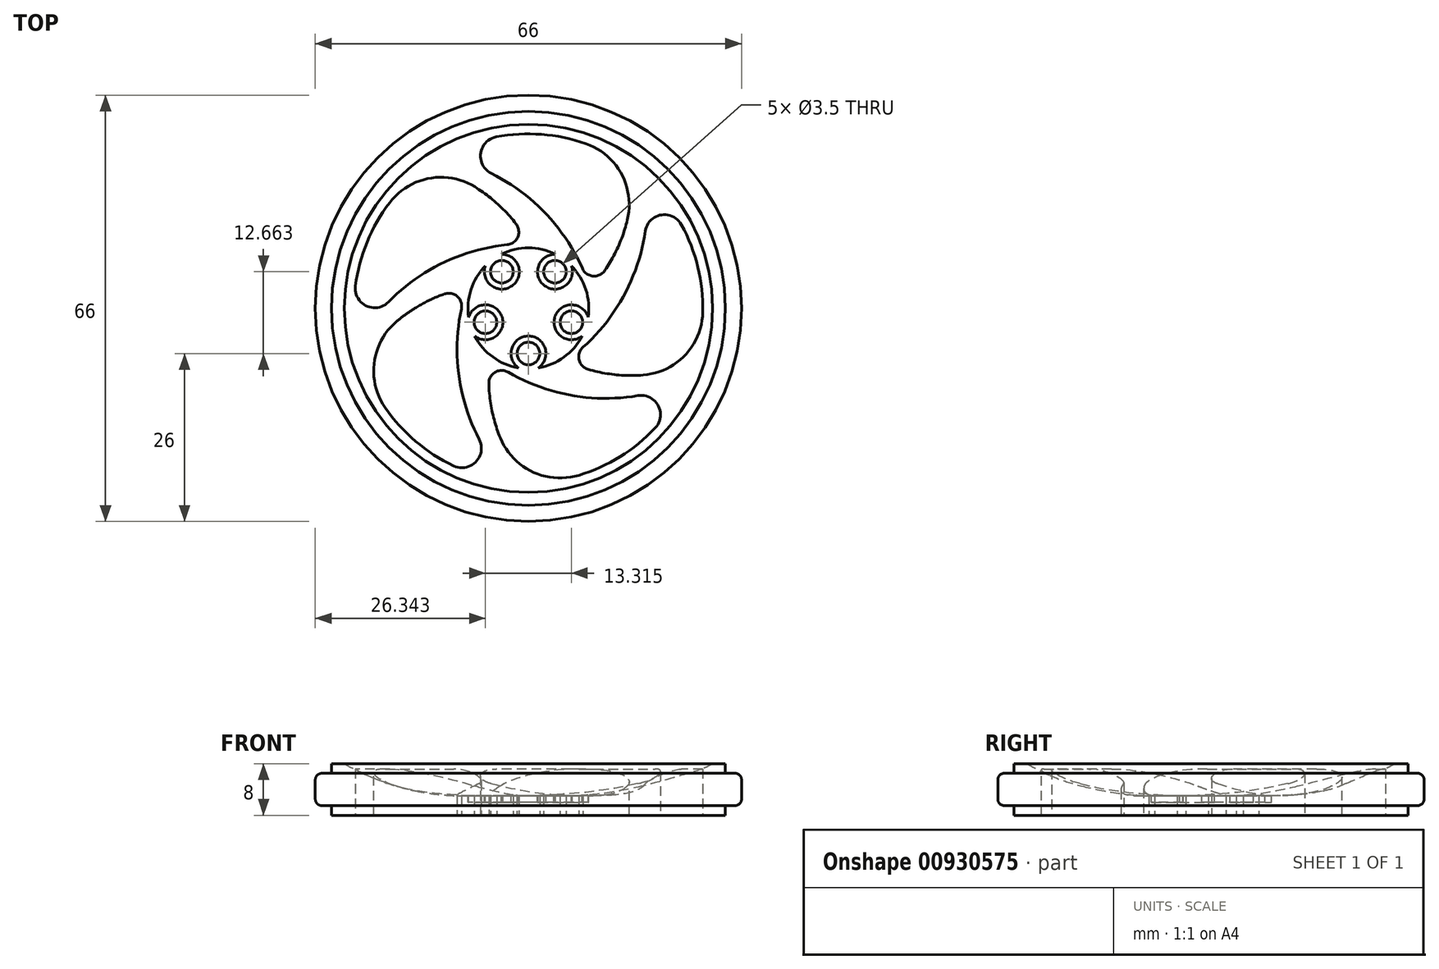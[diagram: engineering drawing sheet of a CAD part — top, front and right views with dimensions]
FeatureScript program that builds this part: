
annotation { "Feature Type Name" : "Feature", "Feature Type Description" : "" }
export const myFeature = defineFeature(function(context is Context, id is Id, definition is map)
    precondition{}
    {
        {
            var Q0;
            Q0=qCreatedBy(makeId("Front.planeOp"),FACE);
            var sketch = newSketch(context, id + "F0", { "sketchPlane" : qUnion([Q0])});
            skLineSegment(sketch, "E0.right", {"start": v(33, 1.5) * mm, "end": v(33, 6.5) * mm});
            skLineSegment(sketch, "E1", {"start": v(30.5, 6.5) * mm, "end": v(33, 6.5) * mm});
            skLineSegment(sketch, "E2", {"start": v(30.5, 6.5) * mm, "end": v(30.5, 8) * mm});
            skLineSegment(sketch, "E3.MirrorCS", {"start": v(30.5, 1.5) * mm, "end": v(30.5, 0) * mm});
            skLineSegment(sketch, "E4.MirrorCS", {"start": v(30.5, 1.5) * mm, "end": v(33, 1.5) * mm});
            skLineSegment(sketch, "E5.trimOffspring", {"start": v(28.5, 8) * mm, "end": v(30.5, 8) * mm});
            skLineSegment(sketch, "E6", {"start": v(0, 0) * mm, "end": v(30.5, 0) * mm});
            skLineSegment(sketch, "E7", {"start": v(0, 0) * mm, "end": v(0, 3) * mm});
            skLineSegment(sketch, "E8", {"start": v(0, 3) * mm, "end": v(10, 3) * mm});
            skArc(sketch, "E9", {"start": v(10, 3) * mm, "mid": v(19.58, 4.27) * mm, "end": v(28.5, 8) * mm});
            skSolve(sketch);
        }
        {
            var Q0;
            Q0=qSketchRegion(id+"F0",true);
            var Q1;
            Q1=sQuery(id+"F0.wireOp",EDGE,"E7");
            revolve(context, id + "F1", {"entities" : qUnion([Q0]), "axis" : qUnion([Q1]), "revolveType" : RevolveType.FULL});
        }
        {
            var Q0;
            Q0=makeQuery(id+"F1.opRevolve","SWEPT_EDGE",EDGE,{"disambiguationData":[OSD([sQuery(id+"F0.wireOp",EDGE,"E0.right"),sQuery(id+"F0.wireOp",EDGE,"E1")])]});
            var Q1;
            Q1=makeQuery(id+"F1.opRevolve","SWEPT_EDGE",EDGE,{"disambiguationData":[OSD([sQuery(id+"F0.wireOp",EDGE,"E0.right"),sQuery(id+"F0.wireOp",EDGE,"E4.MirrorCS")])]});
            fillet(context, id + "F2", {"entities" : qUnion([Q0, Q1]), "radius" : 1 * mm, "tangentPropagation" : true, "allowEdgeOverflow" : false});
        }
        {
            var Q0;
            Q0=makeQuery(id+"F1.opRevolve","SWEPT_FACE",FACE,{"disambiguationData":[OSD([sQuery(id+"F0.wireOp",EDGE,"E6")])]});
            var sketch = newSketch(context, id + "F3", { "sketchPlane" : qUnion([Q0])});
            skCircle(sketch, "E10", {"center": v(0, 0) * mm, "radius": 10 * mm, "construction": true});
            skCircle(sketch, "E11", {"center": v(0, 0) * mm, "radius": 28.5 * mm, "construction": true});
            skArc(sketch, "E12", {"start": v(-3, 26.83) * mm, "mid": v(-17.06, 20.93) * mm, "end": v(-25.68, 8.34) * mm});
            skArc(sketch, "E13.trimOffspring", {"start": v(-26.45, 5.44) * mm, "mid": v(-25.18, -9.76) * mm, "end": v(-15.87, -21.84) * mm});
            skArc(sketch, "E14.trimOffspring", {"start": v(18.2, -19.95) * mm, "mid": v(26.1, -6.9) * mm, "end": v(25.68, 8.34) * mm});
            skLineSegment(sketch, "E15", {"start": v(0, 28.5) * mm, "end": v(0, 0) * mm, "construction": true});
            skLineSegment(sketch, "E16", {"start": v(0, 0) * mm, "end": v(-25.68, 8.34) * mm, "construction": true});
            skLineSegment(sketch, "E17", {"start": v(0, 0) * mm, "end": v(25.68, 8.34) * mm, "construction": true});
            skLineSegment(sketch, "E18", {"start": v(0, 0) * mm, "end": v(-15.87, -21.84) * mm, "construction": true});
            skLineSegment(sketch, "E19", {"start": v(0, 0) * mm, "end": v(15.87, -21.84) * mm, "construction": true});
            skArc(sketch, "E20.trimOffspring", {"start": v(24.6, 11.14) * mm, "mid": v(14.63, 22.7) * mm, "end": v(0, 27) * mm});
            skArc(sketch, "E21.trimOffspring", {"start": v(-13.35, -23.47) * mm, "mid": v(1.5, -26.96) * mm, "end": v(15.87, -21.84) * mm});
            skCircle(sketch, "E22", {"center": v(0, 7) * mm, "radius": 1.75 * mm});
            skCircle(sketch, "E23", {"center": v(-4.11, -5.66) * mm, "radius": 1.75 * mm});
            skCircle(sketch, "E24", {"center": v(4.11, -5.66) * mm, "radius": 1.75 * mm});
            skCircle(sketch, "E25", {"center": v(6.66, 2.16) * mm, "radius": 1.75 * mm});
            skCircle(sketch, "E26", {"center": v(-6.66, 2.16) * mm, "radius": 1.75 * mm});
            skArc(sketch, "E27", {"start": v(-3, 26.83) * mm, "mid": v(-10.37, 12.71) * mm, "end": v(-9.48, -3.2) * mm});
            skArc(sketch, "E28", {"start": v(-26.45, 5.44) * mm, "mid": v(-15.3, -5.93) * mm, "end": v(0.1, -10) * mm});
            skArc(sketch, "E29", {"start": v(-13.35, -23.47) * mm, "mid": v(0.92, -16.38) * mm, "end": v(9.54, -2.99) * mm});
            skArc(sketch, "E30", {"start": v(18.2, -19.95) * mm, "mid": v(15.86, -4.19) * mm, "end": v(5.8, 8.15) * mm});
            skArc(sketch, "E31", {"start": v(24.6, 11.14) * mm, "mid": v(8.89, 13.8) * mm, "end": v(-5.96, 8.03) * mm});
            skArc(sketch, "E32", {"start": v(0, 27) * mm, "mid": v(-5.04, 18.16) * mm, "end": v(-5.96, 8.03) * mm});
            skArc(sketch, "E33", {"start": v(-25.68, 8.34) * mm, "mid": v(-18.83, 0.82) * mm, "end": v(-9.48, -3.2) * mm});
            skArc(sketch, "E34", {"start": v(-15.87, -21.84) * mm, "mid": v(-6.6, -17.65) * mm, "end": v(0.1, -10) * mm});
            skArc(sketch, "E35", {"start": v(15.87, -21.84) * mm, "mid": v(14.75, -11.73) * mm, "end": v(9.54, -2.99) * mm});
            skArc(sketch, "E36", {"start": v(25.68, 8.34) * mm, "mid": v(15.71, 10.4) * mm, "end": v(5.8, 8.15) * mm});
            skSolve(sketch);
        }
        {
            var Q0;
            Q0=qSketchRegion(id+"F3",true);
            extrude(context, id + "F4", {"entities" : qUnion([Q0]), "operationType" : NewBodyOperationType.REMOVE, "oppositeDirection" : true, "depth" : 25 * mm});
        }
        {
            var Q0;
            Q0=makeQuery(id+"F4.boolean.opBoolean","COPY",EDGE,{"derivedFrom":makeQuery(id+"F4.opExtrude","SWEPT_EDGE",EDGE,{"disambiguationData":[OSD([sQuery(id+"F3.wireOp",EDGE,"E12"),sQuery(id+"F3.wireOp",EDGE,"E27")])]})});
            var Q1;
            Q1=makeQuery(id+"F4.boolean.opBoolean","COPY",EDGE,{"derivedFrom":makeQuery(id+"F4.opExtrude","SWEPT_EDGE",EDGE,{"disambiguationData":[OSD([sQuery(id+"F3.wireOp",EDGE,"E20.trimOffspring"),sQuery(id+"F3.wireOp",EDGE,"E31")])]})});
            var Q2;
            Q2=makeQuery(id+"F4.boolean.opBoolean","COPY",EDGE,{"derivedFrom":makeQuery(id+"F4.opExtrude","SWEPT_EDGE",EDGE,{"disambiguationData":[OSD([sQuery(id+"F3.wireOp",EDGE,"E14.trimOffspring"),sQuery(id+"F3.wireOp",EDGE,"E30")])]})});
            var Q3;
            Q3=makeQuery(id+"F4.boolean.opBoolean","COPY",EDGE,{"derivedFrom":makeQuery(id+"F4.opExtrude","SWEPT_EDGE",EDGE,{"disambiguationData":[OSD([sQuery(id+"F3.wireOp",EDGE,"E21.trimOffspring"),sQuery(id+"F3.wireOp",EDGE,"E29")])]})});
            var Q4;
            Q4=makeQuery(id+"F4.boolean.opBoolean","COPY",EDGE,{"derivedFrom":makeQuery(id+"F4.opExtrude","SWEPT_EDGE",EDGE,{"disambiguationData":[OSD([sQuery(id+"F3.wireOp",EDGE,"E13.trimOffspring"),sQuery(id+"F3.wireOp",EDGE,"E28")])]})});
            fillet(context, id + "F5", {"entities" : qUnion([Q0, Q1, Q2, Q3, Q4]), "radius" : 3 * mm, "tangentPropagation" : true, "allowEdgeOverflow" : false});
        }
        {
            var Q0;
            Q0=makeQuery(id+"F4.boolean.opBoolean","COPY",EDGE,{"derivedFrom":makeQuery(id+"F4.opExtrude","SWEPT_EDGE",EDGE,{"disambiguationData":[OSD([sQuery(id+"F3.wireOp",EDGE,"E14.trimOffspring"),sQuery(id+"F3.wireOp",EDGE,"lH133nUo-b4dK-7Uis-ALbx-UH7YrD5dzAr5")])]})});
            var Q1;
            Q1=makeQuery(id+"F4.boolean.opBoolean","COPY",EDGE,{"derivedFrom":makeQuery(id+"F4.opExtrude","SWEPT_EDGE",EDGE,{"disambiguationData":[OSD([sQuery(id+"F3.wireOp",EDGE,"E20.trimOffspring"),sQuery(id+"F3.wireOp",EDGE,"Y5TeA7qx-hglw-YKO1-yJVa-Mu3tWydujS0s")])]})});
            var Q2;
            Q2=makeQuery(id+"F4.boolean.opBoolean","COPY",EDGE,{"derivedFrom":makeQuery(id+"F4.opExtrude","SWEPT_EDGE",EDGE,{"disambiguationData":[OSD([sQuery(id+"F3.wireOp",EDGE,"E12"),sQuery(id+"F3.wireOp",EDGE,"K8Gechwi-EIRI-6laA-ybGk-XkUKvmpAPVkA")])]})});
            var Q3;
            Q3=makeQuery(id+"F4.boolean.opBoolean","COPY",EDGE,{"derivedFrom":makeQuery(id+"F4.opExtrude","SWEPT_EDGE",EDGE,{"disambiguationData":[OSD([sQuery(id+"F3.wireOp",EDGE,"E13.trimOffspring"),sQuery(id+"F3.wireOp",EDGE,"yrZSpx71-NN5u-So2I-DmkD-7K2vPXZf8bNT")])]})});
            var Q4;
            Q4=makeQuery(id+"F4.boolean.opBoolean","COPY",EDGE,{"derivedFrom":makeQuery(id+"F4.opExtrude","SWEPT_EDGE",EDGE,{"disambiguationData":[OSD([sQuery(id+"F3.wireOp",EDGE,"E21.trimOffspring"),sQuery(id+"F3.wireOp",EDGE,"3wq5JMd6-PSVr-Z4Na-BiTl-nTZF3QSmccvR")])]})});
            fillet(context, id + "F6", {"entities" : qUnion([Q0, Q1, Q2, Q3, Q4]), "radius" : 10 * mm, "tangentPropagation" : true, "allowEdgeOverflow" : false});
        }
        {
            var Q0;
            Q0=makeQuery(id+"F4.boolean.opBoolean","COPY",EDGE,{"derivedFrom":makeQuery(id+"F4.opExtrude","SWEPT_EDGE",EDGE,{"disambiguationData":[OSD([sQuery(id+"F3.wireOp",EDGE,"E28"),sQuery(id+"F3.wireOp",EDGE,"E34")])]})});
            var Q1;
            Q1=makeQuery(id+"F4.boolean.opBoolean","COPY",EDGE,{"derivedFrom":makeQuery(id+"F4.opExtrude","SWEPT_EDGE",EDGE,{"disambiguationData":[OSD([sQuery(id+"F3.wireOp",EDGE,"E29"),sQuery(id+"F3.wireOp",EDGE,"E35")])]})});
            var Q2;
            Q2=makeQuery(id+"F4.boolean.opBoolean","COPY",EDGE,{"derivedFrom":makeQuery(id+"F4.opExtrude","SWEPT_EDGE",EDGE,{"disambiguationData":[OSD([sQuery(id+"F3.wireOp",EDGE,"E30"),sQuery(id+"F3.wireOp",EDGE,"E36")])]})});
            var Q3;
            Q3=makeQuery(id+"F4.boolean.opBoolean","COPY",EDGE,{"derivedFrom":makeQuery(id+"F4.opExtrude","SWEPT_EDGE",EDGE,{"disambiguationData":[OSD([sQuery(id+"F3.wireOp",EDGE,"E31"),sQuery(id+"F3.wireOp",EDGE,"E32")])]})});
            var Q4;
            Q4=makeQuery(id+"F4.boolean.opBoolean","COPY",EDGE,{"derivedFrom":makeQuery(id+"F4.opExtrude","SWEPT_EDGE",EDGE,{"disambiguationData":[OSD([sQuery(id+"F3.wireOp",EDGE,"E27"),sQuery(id+"F3.wireOp",EDGE,"E33")])]})});
            fillet(context, id + "F7", {"entities" : qUnion([Q0, Q1, Q2, Q3, Q4]), "radius" : 2 * mm, "tangentPropagation" : true, "allowEdgeOverflow" : false});
        }
        {
            var Q0;
            Q0=makeQuery(id+"F1.opRevolve","SWEPT_FACE",FACE,{"disambiguationData":[OSD([sQuery(id+"F0.wireOp",EDGE,"E8")])]});
            var sketch = newSketch(context, id + "F8", { "sketchPlane" : qUnion([Q0])});
            skArc(sketch, "E37", {"start": v(-6.66, 6.56) * mm, "mid": v(-2.53, 3.48) * mm, "end": v(-4.18, 8.36) * mm});
            skArc(sketch, "E38", {"start": v(4.18, 8.36) * mm, "mid": v(2.53, 3.48) * mm, "end": v(6.66, 6.56) * mm});
            skArc(sketch, "E39", {"start": v(9.25, -1.4) * mm, "mid": v(4.09, -1.33) * mm, "end": v(8.3, -4.3) * mm});
            skArc(sketch, "E40", {"start": v(1.53, -9.22) * mm, "mid": v(0, -4.3) * mm, "end": v(-1.53, -9.22) * mm});
            skArc(sketch, "E41", {"start": v(-8.3, -4.3) * mm, "mid": v(-4.09, -1.33) * mm, "end": v(-9.25, -1.4) * mm});
            skArc(sketch, "E42", {"start": v(-6.66, 6.56) * mm, "mid": v(-8.9, 2.89) * mm, "end": v(-9.25, -1.4) * mm});
            skArc(sketch, "E43.trimOffspring", {"start": v(4.18, 8.36) * mm, "mid": v(0, 9.35) * mm, "end": v(-4.18, 8.36) * mm});
            skArc(sketch, "E44.trimOffspring", {"start": v(9.25, -1.4) * mm, "mid": v(8.9, 2.89) * mm, "end": v(6.66, 6.56) * mm});
            skArc(sketch, "E45.trimOffspring", {"start": v(1.53, -9.22) * mm, "mid": v(5.5, -7.56) * mm, "end": v(8.3, -4.3) * mm});
            skArc(sketch, "E46.trimOffspring", {"start": v(-8.3, -4.3) * mm, "mid": v(-5.5, -7.56) * mm, "end": v(-1.53, -9.22) * mm});
            skSolve(sketch);
        }
        {
            var Q0;
            Q0=qSketchRegion(id+"F8",true);
            extrude(context, id + "F9", {"entities" : qUnion([Q0]), "operationType" : NewBodyOperationType.REMOVE, "oppositeDirection" : true, "depth" : 1 * mm});
        }
    });
